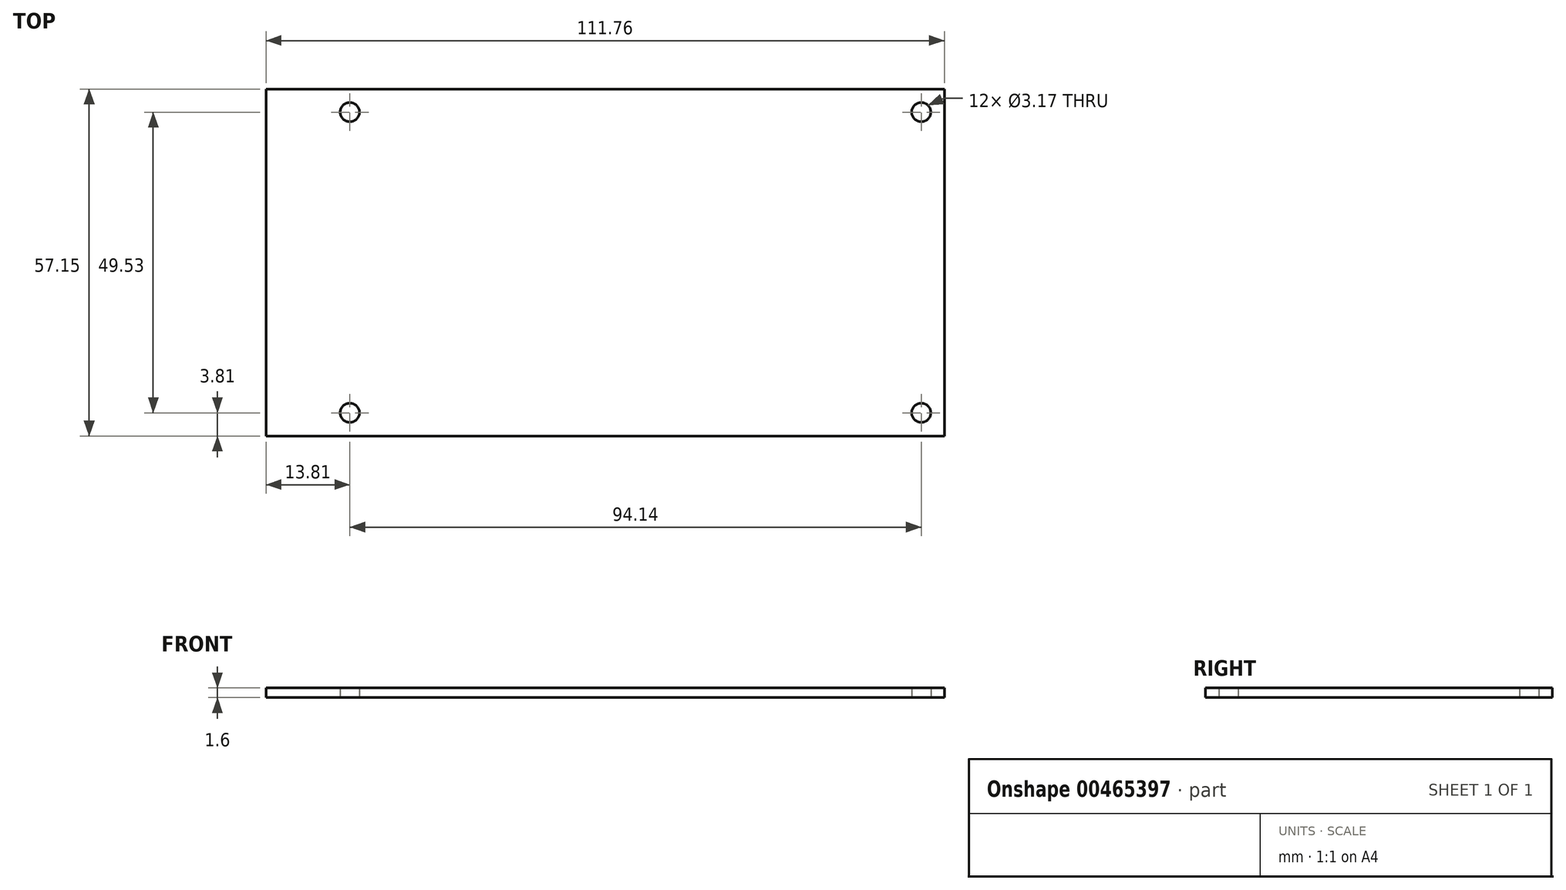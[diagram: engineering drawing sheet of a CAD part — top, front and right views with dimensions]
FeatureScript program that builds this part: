
annotation { "Feature Type Name" : "Feature", "Feature Type Description" : "" }
export const myFeature = defineFeature(function(context is Context, id is Id, definition is map)
    precondition{}
    {
        {
            var Q0;
            Q0=qCreatedBy(makeId("Top.planeOp"),FACE);
            var sketch = newSketch(context, id + "F0", { "sketchPlane" : qUnion([Q0])});
            skLineSegment(sketch, "E0.bottom", {"start": v(0, 0) * mm, "end": v(111.76, 0) * mm});
            skLineSegment(sketch, "E0.top", {"start": v(0, -57.15) * mm, "end": v(111.76, -57.15) * mm});
            skLineSegment(sketch, "E0.left", {"start": v(0, 0) * mm, "end": v(0, -57.15) * mm});
            skLineSegment(sketch, "E0.right", {"start": v(111.76, 0) * mm, "end": v(111.76, -57.15) * mm});
            skCircle(sketch, "E1", {"center": v(13.8, -3.81) * mm, "radius": 1.59 * mm});
            skCircle(sketch, "E2", {"center": v(13.8, -53.34) * mm, "radius": 1.59 * mm});
            skCircle(sketch, "E3", {"center": v(107.95, -53.34) * mm, "radius": 1.59 * mm});
            skCircle(sketch, "E4", {"center": v(107.95, -3.81) * mm, "radius": 1.59 * mm});
            skLineSegment(sketch, "E5", {"start": v(107.95, -3.81) * mm, "end": v(13.8, -3.81) * mm, "construction": true});
            skLineSegment(sketch, "E6", {"start": v(107.95, -53.34) * mm, "end": v(13.8, -53.34) * mm, "construction": true});
            skLineSegment(sketch, "E7", {"start": v(107.95, -53.34) * mm, "end": v(107.95, -3.81) * mm, "construction": true});
            skLineSegment(sketch, "E8", {"start": v(13.8, -53.34) * mm, "end": v(13.8, -3.81) * mm, "construction": true});
            skLineSegment(sketch, "E9", {"start": v(111.76, -28.57) * mm, "end": v(0, -28.57) * mm, "construction": true});
            skPoint(sketch, "E10", {"position": v(107.95, -28.57) * mm});
            skLineSegment(sketch, "E11", {"start": v(10, 0) * mm, "end": v(10, -57.15) * mm, "construction": true});
            skSolve(sketch);
        }
        {
            var Q0;
            Q0=makeQuery(id+"F0.imprint","IMPRINT",FACE,{"disambiguationData":[TD([[makeQuery(id+"F0.imprint","IMPRINT",EDGE,{"derivedFrom":sQuery(id+"F0.wireOp",EDGE,"E0.bottom")}),-1.0]])]});
            extrude(context, id + "F1", {"entities" : qUnion([Q0]), "depth" : 1.6 * mm, "offsetDistance" : 25 * mm});
        }
        {
            var Q0;
            Q0=makeQuery(id+"F1.opExtrude","CAP_FACE",FACE,{"disambiguationData":[OSD([sQuery(id+"F0.wireOp",EDGE,"E0.bottom"),sQuery(id+"F0.wireOp",EDGE,"E0.top"),sQuery(id+"F0.wireOp",EDGE,"E0.left"),sQuery(id+"F0.wireOp",EDGE,"E0.right"),sQuery(id+"F0.wireOp",EDGE,"E1"),sQuery(id+"F0.wireOp",EDGE,"E2"),sQuery(id+"F0.wireOp",EDGE,"E3"),sQuery(id+"F0.wireOp",EDGE,"E4")])],"isStart":false});
            var sketch = newSketch(context, id + "F2", { "sketchPlane" : qUnion([Q0])});
            skPoint(sketch, "E12", {"position": v(83.1, -28.57) * mm});
            skLineSegment(sketch, "E13", {"start": v(83.1, 0) * mm, "end": v(83.1, -57.15) * mm, "construction": true});
            skLineSegment(sketch, "E14", {"start": v(13.8, -3.8) * mm, "end": v(107.95, -53.34) * mm, "construction": true});
            skLineSegment(sketch, "E15", {"start": v(13.8, -53.34) * mm, "end": v(107.95, -3.8) * mm, "construction": true});
            skPoint(sketch, "E16", {"position": v(60.88, -28.57) * mm});
            skLineSegment(sketch, "E17", {"start": v(38.65, 0) * mm, "end": v(38.66, -57.15) * mm, "construction": true});
            skPoint(sketch, "E18", {"position": v(38.66, -28.57) * mm});
            skLineSegment(sketch, "E19", {"start": v(38.66, -28.57) * mm, "end": v(83.1, -28.57) * mm, "construction": true});
            skSolve(sketch);
        }
        {
            var Q0;
            Q0=makeQuery(id+"F1.opExtrude","CAP_FACE",FACE,{"disambiguationData":[OSD([sQuery(id+"F0.wireOp",EDGE,"E0.bottom"),sQuery(id+"F0.wireOp",EDGE,"E0.top"),sQuery(id+"F0.wireOp",EDGE,"E0.left"),sQuery(id+"F0.wireOp",EDGE,"E0.right"),sQuery(id+"F0.wireOp",EDGE,"E1"),sQuery(id+"F0.wireOp",EDGE,"E2"),sQuery(id+"F0.wireOp",EDGE,"E3"),sQuery(id+"F0.wireOp",EDGE,"E4")])],"isStart":true});
            var sketch = newSketch(context, id + "F3", { "sketchPlane" : qUnion([Q0])});
            skLineSegment(sketch, "E20", {"start": v(13.8, 3.8) * mm, "end": v(107.95, 53.34) * mm, "construction": true});
            skLineSegment(sketch, "E21", {"start": v(13.8, 53.34) * mm, "end": v(107.95, 3.8) * mm, "construction": true});
            skLineSegment(sketch, "E22", {"start": v(60.88, 0) * mm, "end": v(60.88, 28.57) * mm, "construction": true});
            skPoint(sketch, "E22.startSnap0", {"position": v(60.88, 28.57) * mm});
            skPoint(sketch, "E23", {"position": v(60.88, 6.35) * mm});
            skLineSegment(sketch, "E24", {"start": v(60.88, 28.57) * mm, "end": v(111.76, 28.57) * mm, "construction": true});
            skPoint(sketch, "E25.MirrorP", {"position": v(60.88, 50.8) * mm});
            skLineSegment(sketch, "E26.bottom", {"start": v(0, 57.15) * mm, "end": v(10.16, 57.15) * mm, "construction": true});
            skLineSegment(sketch, "E26.top", {"start": v(0, 0) * mm, "end": v(10.16, 0) * mm, "construction": true});
            skLineSegment(sketch, "E26.left", {"start": v(0, 57.15) * mm, "end": v(0, 0) * mm, "construction": true});
            skLineSegment(sketch, "E26.right", {"start": v(10.16, 57.15) * mm, "end": v(10.16, 0) * mm, "construction": true});
            skLineSegment(sketch, "E27", {"start": v(0, 28.57) * mm, "end": v(10.16, 28.57) * mm, "construction": true});
            skLineSegment(sketch, "E28", {"start": v(5.08, 28.57) * mm, "end": v(5.08, 0) * mm, "construction": true});
            skPoint(sketch, "E29", {"position": v(5.08, 14.29) * mm});
            skLineSegment(sketch, "E30", {"start": v(5.08, 28.57) * mm, "end": v(5.08, 57.15) * mm, "construction": true});
            skPoint(sketch, "E31", {"position": v(5.08, 42.86) * mm});
            skSolve(sketch);
        }
    });
